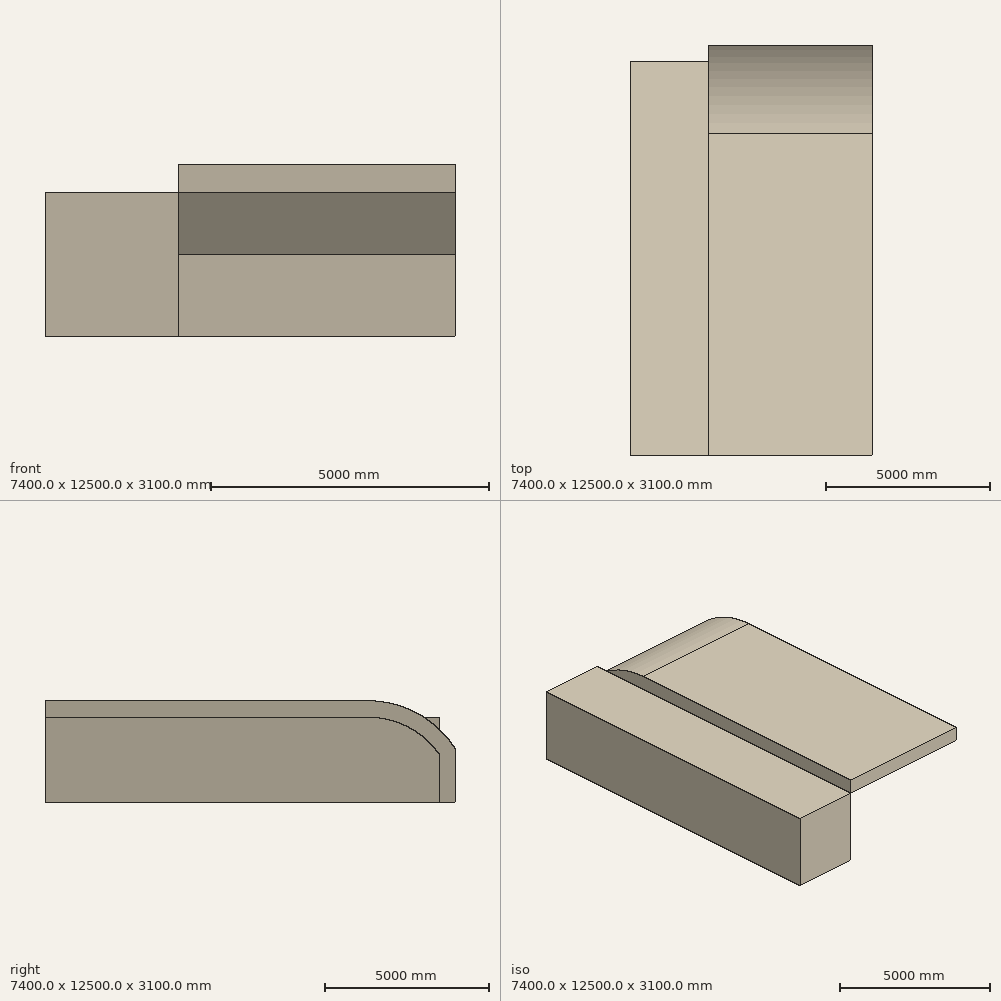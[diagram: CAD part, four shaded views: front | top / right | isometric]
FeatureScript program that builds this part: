
annotation { "Feature Type Name" : "Feature", "Feature Type Description" : "" }
export const myFeature = defineFeature(function(context is Context, id is Id, definition is map)
    precondition{}
    {
        {
            var Q0;
            Q0=qCreatedBy(makeId("Front.planeOp"),FACE);
            var sketch = newSketch(context, id + "F0", { "sketchPlane" : qUnion([Q0])});
            skLineSegment(sketch, "E0.rect.bottom", {"start": v(1200, -1300) * mm, "end": v(-1200, -1300) * mm});
            skLineSegment(sketch, "E0.rect.top", {"start": v(1200, 1300) * mm, "end": v(-1200, 1300) * mm});
            skLineSegment(sketch, "E0.rect.left", {"start": v(1200, -1300) * mm, "end": v(1200, 1300) * mm});
            skLineSegment(sketch, "E0.rect.right", {"start": v(-1200, -1300) * mm, "end": v(-1200, 1300) * mm});
            skPoint(sketch, "E0.rect.middle", {"position": v(0, 0) * mm});
            skSolve(sketch);
        }
        {
            var Q0;
            Q0=qSketchRegion(id+"F0",true);
            extrude(context, id + "F1", {"entities" : qUnion([Q0]), "oppositeDirection" : true, "depth" : 12000 * mm});
        }
        {
            var Q0;
            Q0=makeQuery(id+"F1.opExtrude","SWEPT_FACE",FACE,{"disambiguationData":[OSD([sQuery(id+"F0.wireOp",EDGE,"E0.rect.left")])]});
            var sketch = newSketch(context, id + "F2", { "sketchPlane" : qUnion([Q0])});
            skLineSegment(sketch, "E1", {"start": v(0, 1300) * mm, "end": v(9825.05, 1300) * mm});
            skLineSegment(sketch, "E2", {"start": v(12000, -1300) * mm, "end": v(12000, 173.87) * mm});
            skArc(sketch, "E3", {"start": v(12000, 173.87) * mm, "mid": v(11049.65, 1001.77) * mm, "end": v(9825.05, 1300) * mm});
            skLineSegment(sketch, "E4.0", {"start": v(12500, -1300) * mm, "end": v(12500, 325.27) * mm});
            skArc(sketch, "E4.1", {"start": v(12500, 325.27) * mm, "mid": v(11352.32, 1406.9) * mm, "end": v(9825.05, 1800) * mm});
            skLineSegment(sketch, "E4.2", {"start": v(0, 1800) * mm, "end": v(9825.05, 1800) * mm});
            skLineSegment(sketch, "E5", {"start": v(0, 1800) * mm, "end": v(0, 1300) * mm});
            skLineSegment(sketch, "E6", {"start": v(12000, -1300) * mm, "end": v(12500, -1300) * mm});
            skSolve(sketch);
        }
        {
            var Q0;
            Q0=qSketchRegion(id+"F2",true);
            extrude(context, id + "F3", {"entities" : qUnion([Q0]), "depth" : 5000 * mm});
        }
    });
